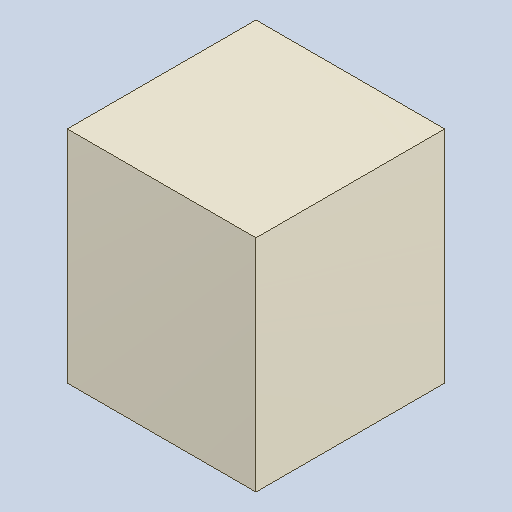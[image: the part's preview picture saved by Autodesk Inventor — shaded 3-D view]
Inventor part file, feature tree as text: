
AUTODESK INVENTOR PART (.ipt)
format: ipt  version: 2023.4 (Build 274418000, 418)  size: 82,944 bytes
history: native  units: mm
features: extrude x1
ambient origin geometry x8: Origin, YZ Plane, XZ Plane, XY Plane, X Axis, Y Axis, Z Axis, Center Point
bodies: Solid1 (feature_tree)
feature tree (1):
  extrude  "Extruded_1"  [1 undecoded]
note: 1 required parameter value undecoded (feature->parameter linkage not recoverable at this tier; creation-order binding heuristic only, values carry confidence <= 0.55)
